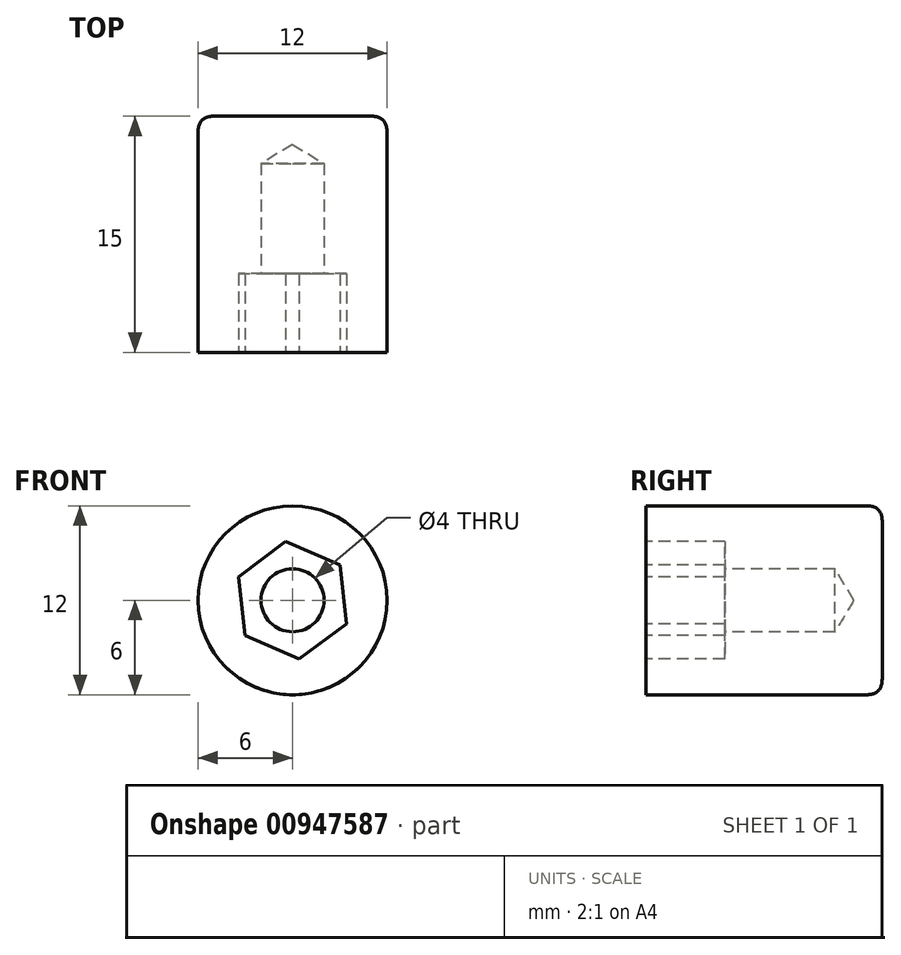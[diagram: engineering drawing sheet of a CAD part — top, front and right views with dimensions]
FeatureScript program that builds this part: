
annotation { "Feature Type Name" : "Feature", "Feature Type Description" : "" }
export const myFeature = defineFeature(function(context is Context, id is Id, definition is map)
    precondition{}
    {
        {
            var Q0;
            Q0=qCreatedBy(makeId("Front.planeOp"),FACE);
            var sketch = newSketch(context, id + "F0", { "sketchPlane" : qUnion([Q0])});
            skCircle(sketch, "E0", {"center": v(0, 0) * mm, "radius": 6 * mm});
            skSolve(sketch);
        }
        {
            var Q0;
            Q0 = qSketchRegion(id + "F0", true);
            extrude(context, id + "F1", {"entities" : qUnion([Q0]), "oppositeDirection" : true, "depth" : 15 * mm, "offsetDistance" : 25 * mm});
        }
        {
            var Q0;
            Q0=sQuery(id+"F0.wireOp",VERTEX,"E0.center");
            var Q1;
            Q1=makeQuery(id+"F1.opExtrude","SWEPT_BODY",BODY,{"disambiguationData":[OSD([sQuery(id+"F0.wireOp",EDGE,"E0")])]});
            hole(context, id + "F2", {"style" : HoleStyle.SIMPLE, "endStyle" : HoleEndStyle.BLIND, "holeDiameter" : 4 * mm, "majorDiameter" : 5 * mm, "holeDepth" : 12 * mm, "isTappedThrough" : true, "tappedDepth" : 12 * mm, "tapClearance" : 3, "locations" : qUnion([Q0]), "scope" : qUnion([Q1])});
        }
        {
            var Q0;
            Q0=makeQuery(id+"F1.opExtrude","CAP_EDGE",EDGE,{"disambiguationData":[OSD([sQuery(id+"F0.wireOp",EDGE,"E0")])],"isStart":false});
            fillet(context, id + "F3", {"entities" : qUnion([Q0]), "radius" : 1 * mm, "tangentPropagation" : true, "rho" : 0.5, "crossSection" : FilletCrossSection.CONIC, "allowEdgeOverflow" : false});
        }
        {
            var Q0;
            Q0=qCreatedBy(makeId("Front.planeOp"),FACE);
            var sketch = newSketch(context, id + "F4", { "sketchPlane" : qUnion([Q0])});
            skCircle(sketch, "E1.cCircle", {"center": v(0, 0) * mm, "radius": 3.25 * mm, "construction": true});
            skLineSegment(sketch, "E1.0", {"start": v(3.44, -1.5) * mm, "end": v(0.43, -3.73) * mm});
            skLineSegment(sketch, "E1.1", {"start": v(0.43, -3.73) * mm, "end": v(-3.01, -2.23) * mm});
            skLineSegment(sketch, "E1.2", {"start": v(-3.01, -2.23) * mm, "end": v(-3.44, 1.5) * mm});
            skLineSegment(sketch, "E1.3", {"start": v(-3.44, 1.5) * mm, "end": v(-0.43, 3.73) * mm});
            skLineSegment(sketch, "E1.4", {"start": v(-0.43, 3.73) * mm, "end": v(3.01, 2.23) * mm});
            skLineSegment(sketch, "E1.5", {"start": v(3.01, 2.23) * mm, "end": v(3.44, -1.5) * mm});
            skPoint(sketch, "E1.0.midPoint", {"position": v(1.94, -2.61) * mm});
            skSolve(sketch);
        }
        {
            var Q0;
            Q0=makeQuery(id+"F4.imprint","IMPRINT",FACE,{"disambiguationData":[TD([[makeQuery(id+"F4.imprint","IMPRINT",EDGE,{"derivedFrom":sQuery(id+"F4.wireOp",EDGE,"E1.0")}),-1.0]])]});
            extrude(context, id + "F5", {"entities" : qUnion([Q0]), "operationType" : NewBodyOperationType.REMOVE, "oppositeDirection" : true, "depth" : 5 * mm, "offsetDistance" : 25 * mm});
        }
    });
